# Revit family: MEFA Trägerklammer PK-PKB
name_source: partatom
category: HLS-Bauteile
revit_build: Autodesk Revit 2017 (Build: 20190507_1515(x64)
units: mm (PartAtom-declared; Revit-internal decimal feet)

## family parameters
Basisbauteil = Fläche
Beim Laden mit Abzugskörper schneiden = Nein
Bemaßung runder Anschluss = Durchmesser verwenden
Gemeinsam genutzt = Ja
Raumberechnungspunkt = Nein
Teiletyp = Normal

## types (6) — shared parameters
Anzugsmoment = 0.00 kip-ft
Fabrikat = Jiangmen Eurofix
Firma = MEFA Befestigungs- und Montagesysteme GmbH
Material = Stahl
Mengeneinheit = St
Oberflaeche = galvanisch verzinkt
Vorgabe-Ansicht = 1219 mm
vpe = 50 St
zero-valued in all types: Stärke

## per-type parameters (varying)
| type | Artikelnummer | Befestigung | DF1 | EAN | Gewicht | Gewicht pro Bauteil | Gewinde | Höhe | Kurztext1 | Kurztext2 | Lochdurchmesser | Typ | max Klemmdicke | max. zul. Last | min. Klemmdicke |
| Durchgangsloch  PKB  8 | 0576801 | mit Durchgangsloch | 10 mm  [stored 0.0328084 ft] | 4250928459022 | 0.05 kg | 0.05 kg | für M8 | 37 mm | Trägerklammer Stahl PKB 8 | Klemmbereich 2 - 20 mm Loch für M8 | 9 mm | MEFA Trägerklammer PKB  8 - M 8 : MEFA Trägerklammer PKB  8 | 0 mm  [stored 0 ft] | 0.27 kip | 2 mm |
| Durchgangsloch  PKB 10 | 0576805 | mit Durchgangsloch | 12 mm  [stored 0.0393701 ft] | 4250928459039 | 0.13 kg | 0.13 kg | für M10 | 44 mm | Trägerklammer Stahl PKB 10 | Klemmbereich 0 - 22 mm Loch für M10 | 11 mm | MEFA Trägerklammer PKB 10 - M10 : MEFA Trägerklammer PKB 10 | 0 mm  [stored 0 ft] | 0.56 kip | 0 mm |
| Durchgangsloch  PK 12 | 0576807 | mit Durchgangsloch | 20 mm  [stored 0.0656168 ft] | 4250928459046 | 0.24 kg | 0.24 kg | für M12 | 61 mm | Trägerklammer Stahl PK 12 | Klemmbereich 8 - 26 mm Loch für M12 | 13 mm | MEFA Trägerklammer PKB 12 - M12 : MEFA Trägerklammer PKB 12 | 0 mm  [stored 0 ft] | 0.79 kip | 8 mm |
| mit Gewinde PKB M 8 | 0576802 | mit Gewinde | 10 mm  [stored 0.0328084 ft] | 4250928459053 | 0.05 kg | 0.05 kg | M8 | 37 mm | Trägerklammer Stahl PKB M8 | Klemmbereich 2 - 20 mm M8 |  | MEFA Trägerklammer PKB  8 - M 8 : MEFA Trägerklammer PKB M 8 | 0 mm  [stored 0 ft] | 0.27 kip | 2 mm |
| mit Gewinde PKB M10 | 0576806 | mit Gewinde | 12 mm  [stored 0.0393701 ft] | 4250928459060 | 0.13 kg | 0.13 kg | M10 | 44 mm | Trägerklammer Stahl PKB M10 | Klemmbereich 0 - 22 mm M10 |  | MEFA Trägerklammer PKB 10 - M10 : MEFA Trägerklammer PKB M10 | 0 mm  [stored 0 ft] | 0.56 kip | 0 mm |
| mit Gewinde PK M12 | 0576808 | mit Gewinde | 20 mm  [stored 0.0656168 ft] | 4250928459077 | 0.24 kg | 0.24 kg | M12 | 61 mm | Trägerklammer Stahl PK M12 | Klemmbereich 8 - 26 mm M12 |  | MEFA Trägerklammer PKB 12 - M12 : MEFA Trägerklammer PKB M12 | 26 mm | 0.79 kip | 8 mm |

note: [stored X ft] marks values corroborated as IEEE doubles in the binary element streams (Revit-internal decimal feet)

## geometry (parser evidence)
native form markers: Sweep x7
no freeform markers — native parametric forms only
